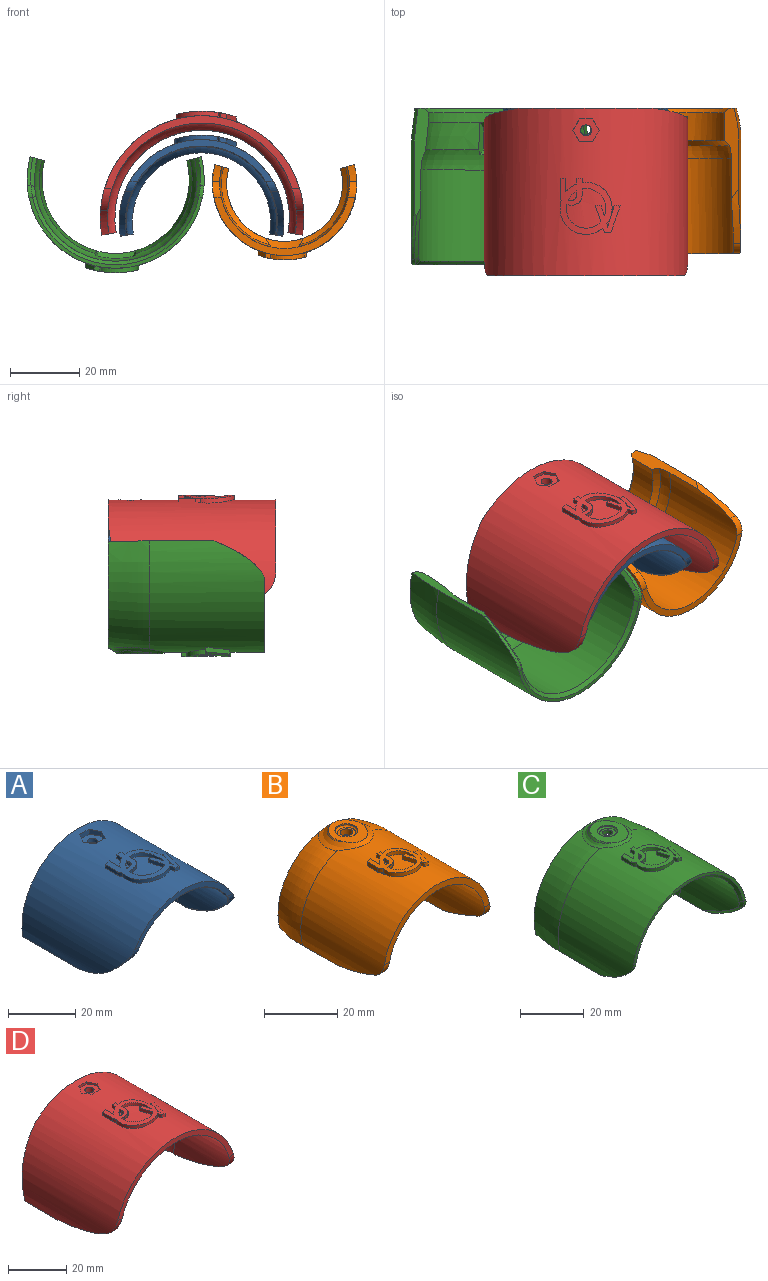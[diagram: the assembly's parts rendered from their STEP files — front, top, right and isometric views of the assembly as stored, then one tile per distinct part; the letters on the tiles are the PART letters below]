
ASSEMBLY  parts=4 mates=3
PART A: 68 faces, bbox 50.4x44.5x29.5 mm
  f0: cylinder r=7.49mm len=3.24mm, axis (0,0,-1), area 5.3mm2, adj f9,f10,f15,f41
  f1: extruded ~1.76x1.49mm, area 2.5mm2, adj f2,f11,f15,f41
  f2: cylinder r=7.49mm len=12.13mm, axis (0,0,-1), area 24.8mm2, adj f1,f3,f15,f41
  f3: plane 1.56x1.41mm, normal (-0.95,-0.32,0), area 2.1mm2, adj f2,f4,f15,f41
  f4: plane 1.94x1.82mm, normal (0,-1,0), area 2.5mm2, adj f3,f5,f15,f41
  f5: plane 8.48x2.95mm, normal (0.95,-0.32,0), area 12mm2, adj f4,f6,f15,f41
  f6: plane 2.09x1.79mm, normal (0,1,0), area 2.5mm2, adj f5,f7,f15,f41
  f7: plane 3.04x1.67mm, normal (-0.95,0.3,0), area 4.2mm2, adj f6,f8,f15,f41
  f8: cylinder r=7.49mm len=9.59mm, axis (0,0,-1), area 19.4mm2, adj f7,f12,f15,f41
  f9: plane 2.13x1.28mm, normal (-1,0,0), area 2.7mm2, adj f0,f14,f15,f41
  f10: plane 4.57x1.31mm, normal (1,0,0), area 6mm2, adj f0,f13,f15,f41
  f11: plane 5.24x1.34mm, normal (-1,0,0), area 7mm2, adj f1,f13,f15,f41
  f12: plane 1.68x1.27mm, normal (1,0,0), area 2.1mm2, adj f8,f14,f15,f41
  f13: plane 1.83x1.72mm, normal (0,1,0), area 2.3mm2, adj f10,f11,f15,f41
  f14: plane 1.72x1.41mm, normal (0,1,0), area 2.2mm2, adj f9,f12,f15,f41
  f15: cylinder r=23.74mm len=47.48mm, axis (0,-1,0), area 3222mm2, adj f0,f1,f2,f3,f4,f5,f6,f7
  f16: cylinder r=1.59mm len=3.18mm, axis (0,0,-1), area 17.7mm2, adj f17,f40
  f17: cone r=20.72mm half-angle=9.5deg, axis (0,1,0), area 333.4mm2, adj f16,f18,f19,f21,f22
  f18: cylinder r=19.93mm len=39.86mm, axis (0,-1,0), area 395.4mm2, adj f17,f21,f22,f33
  f19: cone r=19.93mm half-angle=12.9deg, axis (0,-1,0), area 253mm2, adj f17,f20,f21,f22
  f20: plane 47.48x27.86mm, normal (0,1,0), area 290.4mm2, adj f15,f19,f21,f22
  f21: plane 24.63x3.76mm, normal (-0.17,0,-0.98), area 74.2mm2, adj f15,f17,f18,f19,f20,f32,f33,f65
  f22: plane 24.63x3.76mm, normal (0.17,0,-0.98), area 74.2mm2, adj f15,f17,f18,f19,f20,f28,f33,f65
  f23: plane 41.23x11.96mm, normal (0,-1,0), area 85.9mm2, adj f15,f26,f27,f30
  f24: extruded ~18.3x12.61mm, area 41.2mm2, adj f15,f27,f28,f66
  f25: extruded ~18.3x12.61mm, area 41.2mm2, adj f15,f26,f32,f67
  f26: cylinder r=5.08mm len=3.61mm, axis (1,0,0), area 6.9mm2, adj f15,f23,f25,f31
  f27: cylinder r=5.08mm len=3.61mm, axis (1,0,0), area 6.9mm2, adj f15,f23,f24,f29
  f28: bspline ~20.11x13.06mm, area 8mm2, adj f22,f24,f29,f65,f66
  f29: bspline ~3.07x1.78mm, area 1.2mm2, adj f27,f28,f30,f65
  f30: cone r=21.66mm half-angle=45deg, axis (0,-1,0), area 15.7mm2, adj f23,f29,f31,f65
  f31: bspline ~3.07x1.78mm, area 1.2mm2, adj f26,f30,f32,f65
  f32: bspline ~20.11x13.06mm, area 8mm2, adj f21,f25,f31,f65,f67
  f33: torus R=8.96mm, axis (0,1,0), area 493mm2, adj f18,f21,f22,f65
  f34: plane 3.89x1.9mm, normal (0,-1,0), area 7.3mm2, adj f15,f35,f39,f40
  f35: plane 3.37x1.95mm, normal (0.87,-0.5,0), area 6.6mm2, adj f15,f34,f36,f40
  f36: plane 3.37x1.95mm, normal (0.87,0.5,0), area 6.6mm2, adj f15,f35,f37,f40
  f37: plane 3.89x1.9mm, normal (0,1,0), area 7.3mm2, adj f15,f36,f38,f40
  f38: plane 3.37x1.95mm, normal (-0.87,0.5,0), area 6.6mm2, adj f15,f37,f39,f40
  f39: plane 3.37x1.95mm, normal (-0.87,-0.5,0), area 6.6mm2, adj f15,f34,f38,f40
  f40: plane 7.77x6.73mm, normal (0,0,1), area 31.3mm2, adj f16,f34,f35,f36,f37,f38,f39
  f41: cylinder r=25.01mm len=17.63mm, axis (0,-1,0), area 123.3mm2, adj f0,f1,f2,f3,f4,f5,f6,f7
  f42: cylinder r=23.74mm len=11.43mm, axis (0,-1,0), area 82.2mm2, adj f43,f44,f45,f46,f47,f48,f49,f50
  f43: plane 1.79x1.52mm, normal (0,1,0), area 2.3mm2, adj f41,f42,f44,f52
  f44: plane 3.35x1.51mm, normal (0.95,0.3,0), area 4.5mm2, adj f41,f42,f43,f45
  f45: cylinder r=5.71mm len=8.14mm, axis (0,0,-1), area 16.1mm2, adj f41,f42,f44,f46
  f46: plane 1.78x1.27mm, normal (1,0,0), area 2.3mm2, adj f41,f42,f45,f47
  f47: extruded ~1.58x1.29mm, area 2.1mm2, adj f41,f42,f46,f48
  f48: extruded ~1.37x1.17mm, area 2mm2, adj f41,f42,f47,f49
  f49: extruded ~1.8x1.54mm, area 2.4mm2, adj f41,f42,f48,f50
  f50: extruded ~1.56x1.25mm, area 1.6mm2, adj f41,f42,f49,f51
  f51: cylinder r=5.71mm len=9.73mm, axis (0,0,-1), area 18.7mm2, adj f41,f42,f50,f52
  f52: plane 5x1.7mm, normal (-0.95,-0.32,0), area 6.7mm2, adj f41,f42,f43,f51
  f53: cylinder r=23.74mm len=3.46mm, axis (0,-1,0), area 1mm2, adj f54,f55,f56,f57,f58
  f54: extruded ~1.34x0.42mm, area 0.6mm2, adj f41,f53,f55,f58
  f55: extruded ~1.36x0.82mm, area 1.1mm2, adj f41,f53,f54,f56
  f56: extruded ~1.84x1.43mm, area 2.5mm2, adj f41,f53,f55,f57
  f57: plane 1.62x1.48mm, normal (-0.95,0.3,0), area 2.2mm2, adj f41,f53,f56,f58
  f58: cylinder r=7.49mm len=2.23mm, axis (0,0,-1), area 3.4mm2, adj f41,f53,f54,f57
  f59: cylinder r=23.74mm len=2.71mm, axis (0,-1,0), area 2.8mm2, adj f60,f61,f62,f63,f64
  f60: extruded ~1.46x0.83mm, area 1.1mm2, adj f41,f59,f61,f64
  f61: extruded ~1.48x1.23mm, area 1.7mm2, adj f41,f59,f60,f62
  f62: extruded ~1.39x1.33mm, area 1.9mm2, adj f41,f59,f61,f63
  f63: plane 1.28x0.88mm, normal (-1,0,0), area 1.1mm2, adj f41,f59,f62,f64
  f64: cylinder r=5.71mm len=2.57mm, axis (0,0,-1), area 4.6mm2, adj f41,f59,f60,f63
  f65: cylinder r=21.66mm len=43.31mm, axis (0,1,0), area 1603.8mm2, adj f21,f22,f28,f29,f30,f31,f32,f33
  f66: bspline ~6.85x5.56mm, area 3.6mm2, adj f15,f22,f24,f28
  f67: bspline ~6.85x5.56mm, area 3.6mm2, adj f15,f21,f25,f32
PART B: 67 faces, bbox 43.2x44.7x29 mm
  f0: revolved ~25.78x16.92mm, area 309.7mm2, adj f1,f3,f25,f64
  f1: cylinder r=20.74mm len=41.48mm, axis (0,1,0), area 2150.9mm2, adj f0,f2,f3,f4,f6,f7,f8,f9
  f2: plane 26.2x4.12mm, normal (-0.26,0,-0.97), area 67.9mm2, adj f1,f5,f21,f23,f25,f29,f30,f60
  f3: plane 26.2x4.12mm, normal (0.26,0,-0.97), area 67.9mm2, adj f0,f1,f5,f23,f25,f29,f31,f61
  f4: plane 40.69x16.71mm, normal (0,-1,0), area 109.4mm2, adj f1,f5,f62,f63
  f5: cylinder r=18.71mm len=37.41mm, axis (0,1,0), area 1849.9mm2, adj f2,f3,f4,f22,f26,f27,f28,f60
  f6: plane 1.39x1.3mm, normal (0,1,0), area 1.7mm2, adj f1,f7,f20,f36
  f7: plane 1.28x0.93mm, normal (1,0,0), area 1.2mm2, adj f1,f6,f8,f36
  f8: cylinder r=5.71mm len=6.9mm, axis (0,0,-1), area 14.3mm2, adj f1,f7,f9,f36
  f9: plane 1.95x1.49mm, normal (-0.95,0.3,0), area 2.7mm2, adj f1,f8,f10,f36
  f10: plane 1.79x1.36mm, normal (0,1,0), area 1.8mm2, adj f1,f9,f11,f36
  f11: plane 6.4x2.21mm, normal (0.95,-0.32,0), area 8.8mm2, adj f1,f10,f12,f36
  f12: plane 1.62x1.47mm, normal (0,-1,0), area 1.9mm2, adj f1,f11,f13,f36
  f13: plane 1.34x0.97mm, normal (-0.95,-0.32,0), area 1.3mm2, adj f1,f12,f14,f36
  f14: cylinder r=5.71mm len=9.38mm, axis (0,0,-1), area 18.2mm2, adj f1,f13,f15,f36
  f15: extruded ~1.61x1.52mm, area 2.4mm2, adj f1,f14,f16,f36
  f16: plane 3.97x1.35mm, normal (-1,0,0), area 5.4mm2, adj f1,f15,f17,f36
  f17: plane 1.69x1.3mm, normal (0,1,0), area 1.7mm2, adj f1,f16,f18,f36
  f18: plane 3.64x1.32mm, normal (1,0,0), area 4.8mm2, adj f1,f17,f19,f36
  f19: cylinder r=5.71mm len=2.45mm, axis (0,0,-1), area 4.4mm2, adj f1,f18,f20,f36
  f20: plane 1.37x1.29mm, normal (-1,0,0), area 1.8mm2, adj f1,f6,f19,f36
  f21: revolved ~25.78x16.92mm, area 309.7mm2, adj f1,f2,f25,f64
  f22: cylinder r=1.71mm len=3.43mm, axis (0,0,-1), area 22mm2, adj f5,f24,f26
  f23: cylinder r=16.68mm len=33.35mm, axis (0,-1,0), area 409.8mm2, adj f2,f3,f26,f27,f28,f29,f30,f31
  f24: revolved ~5.1x5.09mm, area 11.2mm2, adj f22,f35
  f25: plane 39.07x24.82mm, normal (0,1,0), area 109.9mm2, adj f0,f2,f3,f21,f29,f64
  f26: cone r=18.71mm half-angle=34.2deg, axis (0,-1,0), area 35mm2, adj f5,f22,f23,f27,f28
  f27: plane 12.34x2.75mm, normal (-0.87,0,-0.5), area 19.6mm2, adj f5,f23,f26,f30,f66
  f28: plane 12.34x2.75mm, normal (0.87,0,-0.5), area 19.6mm2, adj f5,f23,f26,f31,f65
  f29: cone r=17.95mm half-angle=45deg, axis (0,1,0), area 114mm2, adj f2,f3,f23,f25
  f30: cone r=16.68mm half-angle=45deg, axis (0,-1,0), area 58.1mm2, adj f2,f23,f27,f66
  f31: cone r=16.68mm half-angle=45deg, axis (0,-1,0), area 58.1mm2, adj f3,f23,f28,f65
  f32: cylinder r=3.11mm len=6.22mm, axis (0,0,-1), area 5.5mm2, adj f33,f35
  f33: plane 13.36x12.02mm, normal (0,0,1), area 59.9mm2, adj f32,f34,f64
  f34: bspline ~10.55x9.19mm, area 0mm2, adj f33,f64
  f35: bspline ~6.23x6.23mm, area 15.6mm2, adj f24,f32
  f36: cylinder r=22.03mm len=13.85mm, axis (0,-1,0), area 69.1mm2, adj f6,f7,f8,f9,f10,f11,f12,f13
  f37: cylinder r=20.74mm len=1.7mm, axis (0,1,0), area 0.3mm2, adj f38,f39,f40,f41,f42
  f38: cylinder r=5.71mm len=1.43mm, axis (0,0,-1), area 1.4mm2, adj f36,f37,f39,f42
  f39: plane 1.31x0.3mm, normal (-0.95,0.3,0), area 0.4mm2, adj f36,f37,f38,f40
  f40: extruded ~1.4x1.37mm, area 1.8mm2, adj f36,f37,f39,f41
  f41: extruded ~1.32x0.62mm, area 0.8mm2, adj f36,f37,f40,f42
  f42: extruded ~1.29x0.12mm, area 0.2mm2, adj f36,f37,f38,f41
  f43: cylinder r=20.74mm len=2.31mm, axis (0,1,0), area 1.7mm2, adj f44,f45,f46,f47,f48
  f44: cylinder r=4.45mm len=2.25mm, axis (0,0,-1), area 3.7mm2, adj f36,f43,f45,f48
  f45: plane 1.29x0.93mm, normal (-1,0,0), area 1.2mm2, adj f36,f43,f44,f46
  f46: extruded ~1.32x1.05mm, area 1.4mm2, adj f36,f43,f45,f47
  f47: extruded ~1.44x0.93mm, area 1.3mm2, adj f36,f43,f46,f48
  f48: extruded ~1.4x0.5mm, area 0.7mm2, adj f36,f43,f44,f47
  f49: cylinder r=20.74mm len=8.89mm, axis (0,1,0), area 49.6mm2, adj f50,f51,f52,f53,f54,f55,f56,f57
  f50: plane 4.07x1.45mm, normal (-0.95,-0.32,0), area 5.4mm2, adj f36,f49,f51,f59
  f51: cylinder r=4.45mm len=7.66mm, axis (0,0,-1), area 14.1mm2, adj f36,f49,f50,f52
  f52: extruded ~1.44x0.7mm, area 0.9mm2, adj f36,f49,f51,f53
  f53: extruded ~1.49x1.37mm, area 1.8mm2, adj f36,f49,f52,f54
  f54: extruded ~1.36x0.88mm, area 1.5mm2, adj f36,f49,f53,f55
  f55: extruded ~1.3x1.2mm, area 1.6mm2, adj f36,f49,f54,f56
  f56: plane 1.75x1.28mm, normal (1,0,0), area 2.2mm2, adj f36,f49,f55,f57
  f57: cylinder r=4.45mm len=6.23mm, axis (0,0,-1), area 12.8mm2, adj f36,f49,f56,f58
  f58: plane 2.78x1.43mm, normal (0.95,0.3,0), area 3.7mm2, adj f36,f49,f57,f59
  f59: plane 1.43x1.36mm, normal (0,1,0), area 1.7mm2, adj f36,f49,f50,f58
  f60: extruded ~15.46x4.8mm, area 30.6mm2, adj f1,f2,f5,f63
  f61: extruded ~15.46x4.8mm, area 30.6mm2, adj f1,f3,f5,f62
  f62: cylinder r=5.08mm len=4.6mm, axis (-1,0,0), area 11.8mm2, adj f1,f4,f5,f61
  f63: cylinder r=5.08mm len=4.6mm, axis (-1,0,0), area 11.8mm2, adj f1,f4,f5,f60
  f64: bspline ~17.52x15.12mm, area 103.3mm2, adj f0,f1,f21,f25,f33,f34
  f65: torus R=6.01mm, axis (0,1,0), area 107.1mm2, adj f3,f5,f28,f31
  f66: torus R=6.01mm, axis (0,1,0), area 107.1mm2, adj f2,f5,f27,f30
PART C: 74 faces, bbox 51.3x45.5x34.7 mm
  f0: plane 1.43x1.37mm, normal (0,1,0), area 1.8mm2, adj f1,f54,f55,f73
  f1: cylinder r=25.48mm len=50.96mm, axis (0,1,0), area 2773.6mm2, adj f0,f2,f29,f30,f31,f32,f33,f34
  f2: cylinder r=5.08mm len=3.48mm, axis (1,0,0), area 4mm2, adj f1,f3,f29,f37
  f3: bspline ~3.48x2.12mm, area 4.8mm2, adj f2,f4,f7,f28
  f4: cone r=23.45mm half-angle=45deg, axis (0,-1,0), area 93.8mm2, adj f3,f5,f7,f37
  f5: bspline ~3.48x2.12mm, area 4.8mm2, adj f4,f6,f7,f36
  f6: bspline ~15.91x9.78mm, area 23.9mm2, adj f5,f7,f34,f35
  f7: cylinder r=23.45mm len=46.89mm, axis (0,1,0), area 2113.2mm2, adj f3,f4,f5,f6,f8,f28,f30,f34
  f8: torus R=10.75mm, axis (0,1,0), area 487.5mm2, adj f7,f9,f24,f25,f26,f27,f30,f34
  f9: cone r=21.21mm half-angle=6.1deg, axis (0,-1,0), area 269.1mm2, adj f8,f10,f24,f30
  f10: cylinder r=21.21mm len=42.42mm, axis (0,-1,0), area 209.3mm2, adj f9,f11,f13,f27,f30,f34
  f11: cone r=22.48mm half-angle=45deg, axis (0,1,0), area 143.8mm2, adj f10,f12,f30,f34
  f12: plane 49.13x31.06mm, normal (0,1,0), area 163.6mm2, adj f11,f30,f31,f32,f33,f34
  f13: cone r=21.21mm half-angle=49.7deg, axis (0,-1,0), area 33.6mm2, adj f10,f14,f22,f23,f24,f26
  f14: cylinder r=23.7mm len=9.65mm, axis (0,-1,0), area 50.1mm2, adj f13,f15,f22,f23,f24,f25,f26
  f15: cylinder r=1.59mm len=3.18mm, axis (0,0,-1), area 16.4mm2, adj f14,f16
  f16: revolved ~5.26x4.79mm, area 12.8mm2, adj f15,f17,f21
  f17: bspline ~4.48x1.27mm, area 2.8mm2, adj f16,f18,f21
  f18: plane 13.4x11.37mm, normal (0,0,1), area 84mm2, adj f17,f19,f20,f32
  f19: cylinder r=3.17mm len=6.35mm, axis (0,0,-1), area 0mm2, adj f18,f21
  f20: bspline ~12.26x12.23mm, area 24.3mm2, adj f18,f32
  f21: bspline ~6.35x5.76mm, area 12.8mm2, adj f16,f17,f19
  f22: plane 5.59x0.59mm, normal (0.98,0,0.2), area 1.5mm2, adj f13,f14,f24
  f23: plane 5.59x0.59mm, normal (-0.98,0,0.2), area 1.5mm2, adj f13,f14,f26
  f24: bspline ~9.96x3.08mm, area 19.1mm2, adj f8,f9,f13,f14,f22,f25
  f25: cone r=23.95mm half-angle=45deg, axis (0,1,0), area 16mm2, adj f8,f14,f24,f26
  f26: bspline ~9.96x3.08mm, area 19.1mm2, adj f8,f13,f14,f23,f25,f27
  f27: cone r=21.21mm half-angle=6.1deg, axis (0,-1,0), area 269.1mm2, adj f8,f10,f26,f34
  f28: bspline ~15.91x9.78mm, area 23.9mm2, adj f3,f7,f29,f30
  f29: extruded ~13.17x8.18mm, area 11.8mm2, adj f1,f2,f28,f30
  f30: plane 31.05x4.32mm, normal (0.26,0,-0.97), area 80.9mm2, adj f1,f7,f8,f9,f10,f11,f12,f28
  f31: revolved ~32.04x24mm, area 471.8mm2, adj f1,f12,f30,f32
  f32: bspline ~17.53x15.26mm, area 80.3mm2, adj f1,f12,f18,f20,f31,f33
  f33: revolved ~32.04x24mm, area 471.8mm2, adj f1,f12,f32,f34
  f34: plane 31.05x4.32mm, normal (-0.26,0,-0.97), area 80.9mm2, adj f1,f6,f7,f8,f10,f11,f12,f27
  f35: extruded ~13.17x8.18mm, area 11.8mm2, adj f1,f6,f34,f36
  f36: cylinder r=5.08mm len=3.48mm, axis (1,0,0), area 4mm2, adj f1,f5,f35,f37
  f37: plane 49.94x20.42mm, normal (0,-1,0), area 69.3mm2, adj f1,f2,f4,f36
  f38: extruded ~1.3x0.05mm, area 0.1mm2, adj f1,f39,f53,f55
  f39: plane 4.15x1.3mm, normal (1,0,0), area 5.4mm2, adj f1,f38,f40,f55
  f40: plane 1.64x1.43mm, normal (0,1,0), area 1.9mm2, adj f1,f39,f41,f55
  f41: plane 4.37x1.31mm, normal (-1,0,0), area 5.7mm2, adj f1,f40,f42,f55
  f42: extruded ~1.66x1.45mm, area 2.3mm2, adj f1,f41,f43,f55
  f43: cylinder r=6.35mm len=10.55mm, axis (0,0,-1), area 21.2mm2, adj f1,f42,f44,f55
  f44: plane 1.36x1.23mm, normal (-0.95,-0.32,0), area 1.7mm2, adj f1,f43,f45,f55
  f45: plane 1.64x1.61mm, normal (0,-1,0), area 2.1mm2, adj f1,f44,f46,f55
  f46: plane 7.03x2.42mm, normal (0.95,-0.32,0), area 9.8mm2, adj f1,f45,f47,f55
  f47: plane 1.8x1.49mm, normal (0,1,0), area 2mm2, adj f1,f46,f48,f55
  f48: plane 4.17x1.66mm, normal (-0.95,0.3,0), area 5.7mm2, adj f1,f47,f49,f55
  f49: extruded ~1.54x1.38mm, area 2.1mm2, adj f1,f48,f50,f55
  f50: extruded ~1.33x0.68mm, area 0.9mm2, adj f1,f49,f51,f55
  f51: extruded ~1.32x0.36mm, area 0.5mm2, adj f1,f50,f52,f55
  f52: cylinder r=6.35mm len=10.01mm, axis (0,0,-1), area 19.2mm2, adj f1,f51,f54,f55
  f53: cylinder r=6.35mm len=2.7mm, axis (0,0,-1), area 4.5mm2, adj f1,f38,f55,f73
  f54: plane 1.57x1.27mm, normal (1,0,0), area 2mm2, adj f0,f1,f52,f55
  f55: cylinder r=26.75mm len=15.25mm, axis (0,-1,0), area 87.5mm2, adj f0,f38,f39,f40,f41,f42,f43,f44
  f56: plane 1.49x1.45mm, normal (0,1,0), area 1.9mm2, adj f55,f57,f58,f66
  f57: cylinder r=25.48mm len=9.65mm, axis (0,1,0), area 60.4mm2, adj f56,f58,f59,f60,f61,f62,f63,f64
  f58: plane 2.58x1.42mm, normal (0.95,0.3,0), area 3.5mm2, adj f55,f56,f57,f59
  f59: cylinder r=4.83mm len=6.41mm, axis (0,0,-1), area 13.2mm2, adj f55,f57,f58,f60
  f60: plane 1.27x1.26mm, normal (1,0,0), area 1.6mm2, adj f55,f57,f59,f61
  f61: extruded ~1.32x1.29mm, area 1.7mm2, adj f55,f57,f60,f62
  f62: extruded ~1.34x0.97mm, area 1.7mm2, adj f55,f57,f61,f63
  f63: extruded ~1.5x1.46mm, area 2mm2, adj f55,f57,f62,f64
  f64: extruded ~1.43x0.82mm, area 1.1mm2, adj f55,f57,f63,f65
  f65: cylinder r=4.83mm len=8.48mm, axis (0,0,-1), area 16.4mm2, adj f55,f57,f64,f66
  f66: plane 4.15x1.45mm, normal (-0.95,-0.32,0), area 5.6mm2, adj f55,f56,f57,f65
  f67: extruded ~1.36x0.44mm, area 0.6mm2, adj f55,f68,f69,f72
  f68: cylinder r=25.48mm len=1.96mm, axis (0,1,0), area 1.3mm2, adj f67,f69,f70,f71,f72
  f69: extruded ~1.41x1.02mm, area 1.4mm2, adj f55,f67,f68,f70
  f70: extruded ~1.31x1.16mm, area 1.6mm2, adj f55,f68,f69,f71
  f71: plane 1.28x0.43mm, normal (-1,0,0), area 0.6mm2, adj f55,f68,f70,f72
  f72: cylinder r=4.83mm len=1.92mm, axis (0,0,-1), area 3.4mm2, adj f55,f67,f68,f71
  f73: plane 2x1.28mm, normal (-1,0,0), area 2.5mm2, adj f0,f1,f53,f55
PART D: 64 faces, bbox 59.2x48.4x35.9 mm
  f0: cylinder r=7.49mm len=3.04mm, axis (0,0,-1), area 4.9mm2, adj f12,f13,f18,f42
  f1: extruded ~1.41x1.39mm, area 1.9mm2, adj f2,f14,f18,f42
  f2: cylinder r=7.49mm len=12.35mm, axis (0,0,-1), area 25.2mm2, adj f1,f3,f18,f42
  f3: plane 1.39x1.37mm, normal (-0.95,-0.32,0), area 1.9mm2, adj f2,f4,f18,f42
  f4: plane 1.82x1.69mm, normal (0,-1,0), area 2.4mm2, adj f3,f5,f18,f42
  f5: plane 7.92x2.73mm, normal (0.95,-0.32,0), area 11mm2, adj f4,f6,f18,f42
  f6: plane 1.86x1.68mm, normal (0,1,0), area 2.2mm2, adj f5,f7,f18,f42
  f7: plane 4.7x1.71mm, normal (-0.95,0.3,0), area 6.4mm2, adj f6,f8,f18,f42
  f8: extruded ~1.73x1.39mm, area 2.3mm2, adj f7,f9,f18,f42
  f9: extruded ~1.33x0.77mm, area 1mm2, adj f8,f10,f18,f42
  f10: extruded ~1.32x0.37mm, area 0.5mm2, adj f9,f11,f18,f42
  f11: cylinder r=7.49mm len=12mm, axis (0,0,-1), area 22.8mm2, adj f10,f15,f18,f42
  f12: plane 1.71x1.28mm, normal (-1,0,0), area 2.2mm2, adj f0,f17,f18,f42
  f13: plane 3.95x1.29mm, normal (1,0,0), area 5.1mm2, adj f0,f16,f18,f42
  f14: plane 4.92x1.31mm, normal (-1,0,0), area 6.5mm2, adj f1,f16,f18,f42
  f15: plane 1.27x1.26mm, normal (1,0,0), area 1.6mm2, adj f11,f17,f18,f42
  f16: plane 1.67x1.61mm, normal (0,1,0), area 2.1mm2, adj f13,f14,f18,f42
  f17: plane 1.62x1.38mm, normal (0,1,0), area 2.1mm2, adj f12,f15,f18,f42
  f18: cylinder r=29.3mm len=58.59mm, axis (0,-1,0), area 4373.8mm2, adj f0,f1,f2,f3,f4,f5,f6,f7
  f19: cylinder r=1.59mm len=3.18mm, axis (0,0,-1), area 24.2mm2, adj f20,f21,f41
  f20: cone r=25.1mm half-angle=12.3deg, axis (0,-1,0), area 337.2mm2, adj f19,f21,f22,f25,f26,f30,f31
  f21: cone r=25.99mm half-angle=12.3deg, axis (0,1,0), area 366.5mm2, adj f19,f20,f24,f25,f26
  f22: cylinder r=25.1mm len=45.94mm, axis (0,-1,0), area 74.4mm2, adj f20,f23,f30,f31
  f23: plane 39.18x7.51mm, normal (0,1,0), area 145.8mm2, adj f18,f22,f30,f31
  f24: cylinder r=25.1mm len=50.21mm, axis (0,-1,0), area 453.5mm2, adj f21,f25,f26,f34
  f25: plane 18.31x4.28mm, normal (-0.17,0,-0.98), area 58.3mm2, adj f18,f20,f21,f24,f29,f31,f34,f63
  f26: plane 18.31x4.28mm, normal (0.17,0,-0.98), area 58.3mm2, adj f18,f20,f21,f24,f28,f30,f34,f63
  f27: plane 56.18x20.98mm, normal (0,-1,0), area 149.7mm2, adj f18,f32,f33,f63
  f28: extruded ~25.77x7.04mm, area 53.1mm2, adj f18,f26,f33,f63
  f29: extruded ~25.77x7.04mm, area 53.1mm2, adj f18,f25,f32,f63
  f30: plane 27.12x17.07mm, normal (0,0.99,-0.15), area 123.9mm2, adj f18,f20,f22,f23,f26
  f31: plane 27.12x17.07mm, normal (0,0.99,-0.15), area 123.9mm2, adj f18,f20,f22,f23,f25
  f32: cylinder r=7.62mm len=6.36mm, axis (1,0,0), area 16.1mm2, adj f18,f27,f29,f63
  f33: cylinder r=7.62mm len=6.36mm, axis (1,0,0), area 16.1mm2, adj f18,f27,f28,f63
  f34: torus R=19.59mm, axis (0,1,0), area 510.9mm2, adj f24,f25,f26,f60,f61,f62,f63
  f35: plane 3.81x0.92mm, normal (0,-1,0), area 3.4mm2, adj f18,f36,f40,f41
  f36: plane 3.31x1.91mm, normal (0.87,-0.5,0), area 3mm2, adj f18,f35,f37,f41
  f37: plane 3.31x1.91mm, normal (0.87,0.5,0), area 3mm2, adj f18,f36,f38,f41
  f38: plane 3.81x0.92mm, normal (0,1,0), area 3.4mm2, adj f18,f37,f39,f41
  f39: plane 3.31x1.91mm, normal (-0.87,0.5,0), area 3mm2, adj f18,f38,f40,f41
  f40: plane 3.31x1.91mm, normal (-0.87,-0.5,0), area 3mm2, adj f18,f35,f39,f41
  f41: plane 7.63x6.6mm, normal (0,0,1), area 29.9mm2, adj f19,f35,f36,f37,f38,f39,f40
  f42: cylinder r=30.57mm len=17.31mm, axis (0,-1,0), area 116.1mm2, adj f0,f1,f2,f3,f4,f5,f6,f7
  f43: cylinder r=29.3mm len=11.43mm, axis (0,-1,0), area 83.8mm2, adj f44,f45,f46,f47,f48,f49,f50,f51
  f44: plane 1.68x1.48mm, normal (0,1,0), area 2.2mm2, adj f42,f43,f45,f53
  f45: plane 2.97x1.44mm, normal (0.95,0.3,0), area 4mm2, adj f42,f43,f44,f46
  f46: cylinder r=5.71mm len=7.9mm, axis (0,0,-1), area 15.9mm2, adj f42,f43,f45,f47
  f47: plane 1.87x1.27mm, normal (1,0,0), area 2.4mm2, adj f42,f43,f46,f48
  f48: extruded ~1.49x1.29mm, area 2mm2, adj f42,f43,f47,f49
  f49: extruded ~1.35x1.1mm, area 1.9mm2, adj f42,f43,f48,f50
  f50: extruded ~1.69x1.48mm, area 2.2mm2, adj f42,f43,f49,f51
  f51: extruded ~1.5x1.28mm, area 1.7mm2, adj f42,f43,f50,f52
  f52: cylinder r=5.71mm len=9.94mm, axis (0,0,-1), area 19.1mm2, adj f42,f43,f51,f53
  f53: plane 4.63x1.58mm, normal (-0.95,-0.32,0), area 6.2mm2, adj f42,f43,f44,f52
  f54: cylinder r=29.3mm len=2.71mm, axis (0,-1,0), area 2.8mm2, adj f55,f56,f57,f58,f59
  f55: extruded ~1.43x0.87mm, area 1.2mm2, adj f42,f54,f56,f59
  f56: extruded ~1.42x1.15mm, area 1.6mm2, adj f42,f54,f55,f57
  f57: extruded ~1.31x1.3mm, area 1.8mm2, adj f42,f54,f56,f58
  f58: plane 1.28x1mm, normal (-1,0,0), area 1.3mm2, adj f42,f54,f57,f59
  f59: cylinder r=5.71mm len=2.54mm, axis (0,0,-1), area 4.5mm2, adj f42,f54,f55,f58
  f60: plane 0.39x0.01mm, normal (0.53,0,0.84), area 0mm2, adj f34,f62,f63
  f61: plane 0.39x0.01mm, normal (-0.81,0,0.59), area 0mm2, adj f34,f62,f63
  f62: plane 51.66x18.9mm, normal (0,-1,0), area 0.7mm2, adj f34,f60,f61,f63
  f63: cylinder r=27.21mm len=54.42mm, axis (0,1,0), area 2490mm2, adj f25,f26,f27,f28,f29,f32,f33,f34
PLACE A t=(-0.05,15.71,-13.19)mm
PLACE B rot(axis=(0,1,0),180deg) t=(23.87,10.9,-2.1)mm
PLACE C rot(axis=(0,1,0),180deg) t=(-24.75,11.35,-1.04)mm
PLACE D t=(0.11,15.33,-11.88)mm fixed
MATE planar D.f23 <-> A.f20  axis (0,1,0) through (12.59,8.98,9.9)mm
MATE planar D.f23 <-> C.f12  axis (0,1,0) through (12.59,8.98,9.9)mm
MATE planar D.f23 <-> B.f25  axis (0,1,0) through (-12.37,8.98,9.9)mm
